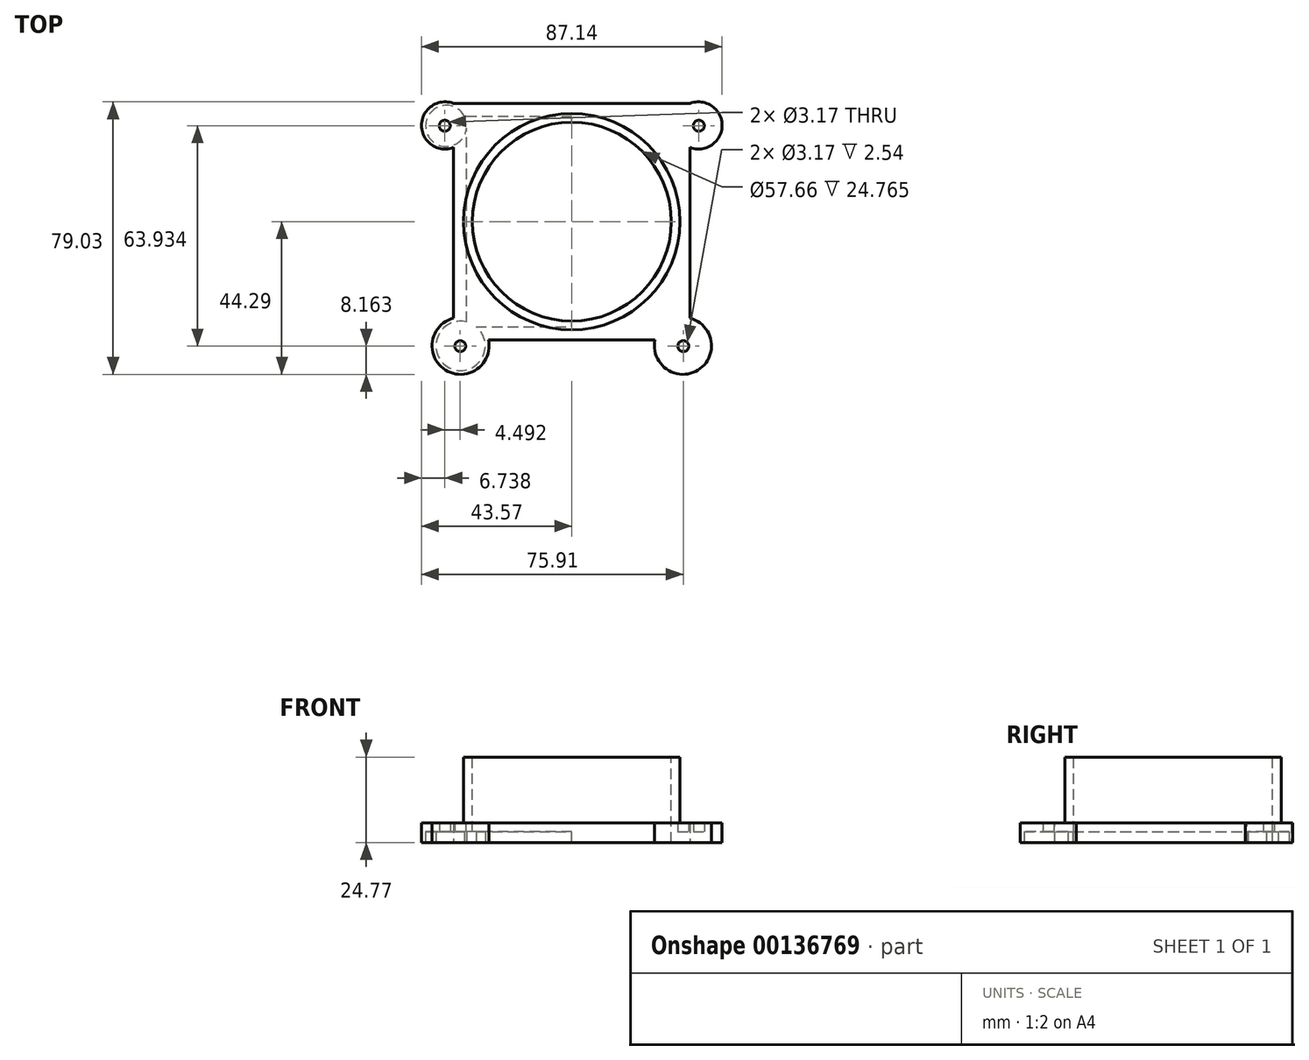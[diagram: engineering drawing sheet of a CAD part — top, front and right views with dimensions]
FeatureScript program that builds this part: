
annotation { "Feature Type Name" : "Feature", "Feature Type Description" : "" }
export const myFeature = defineFeature(function(context is Context, id is Id, definition is map)
    precondition{}
    {
        {
            var Q0;
            Q0=qCreatedBy(makeId("Top.planeOp"),FACE);
            var sketch = newSketch(context, id + "F0", { "sketchPlane" : qUnion([Q0])});
            skLineSegment(sketch, "E0", {"start": v(0, 0) * mm, "end": v(0, 31.75) * mm});
            skLineSegment(sketch, "E1", {"start": v(0, 0) * mm, "end": v(0, -31.75) * mm});
            skLineSegment(sketch, "E2", {"start": v(0, 0) * mm, "end": v(31.75, 0) * mm});
            skLineSegment(sketch, "E3", {"start": v(0, 0) * mm, "end": v(-31.75, 0) * mm});
            skLineSegment(sketch, "E4", {"start": v(0, 31.75) * mm, "end": v(-31.75, 31.75) * mm});
            skLineSegment(sketch, "E5", {"start": v(-31.75, 31.75) * mm, "end": v(-31.75, -31.75) * mm});
            skLineSegment(sketch, "E6", {"start": v(-31.75, -31.75) * mm, "end": v(31.75, -31.75) * mm});
            skLineSegment(sketch, "E7", {"start": v(31.75, -31.75) * mm, "end": v(31.75, 31.75) * mm});
            skLineSegment(sketch, "E8", {"start": v(0, 31.75) * mm, "end": v(31.75, 31.75) * mm});
            skSolve(sketch);
        }
        {
            var Q0;
            Q0 = qSketchRegion(id + "F0", true);
            extrude(context, id + "F1", {"entities" : qUnion([Q0]), "depth" : 2.54 * mm});
        }
        {
            var Q0;
            Q0=makeQuery(id+"F1.opExtrude","CAP_FACE",FACE,{"disambiguationData":[OSD([sQuery(id+"F0.wireOp",EDGE,"E4"),sQuery(id+"F0.wireOp",EDGE,"E5"),sQuery(id+"F0.wireOp",EDGE,"E6"),sQuery(id+"F0.wireOp",EDGE,"E7"),sQuery(id+"F0.wireOp",EDGE,"E8")])],"isStart":false});
            var sketch = newSketch(context, id + "F2", { "sketchPlane" : qUnion([Q0])});
            skCircle(sketch, "E9", {"center": v(0, 0) * mm, "radius": 28.83 * mm});
            skSolve(sketch);
        }
        {
            var Q0;
            Q0 = qSketchRegion(id + "F2", true);
            extrude(context, id + "F3", {"entities" : qUnion([Q0]), "operationType" : NewBodyOperationType.REMOVE, "oppositeDirection" : true, "depth" : 25.4 * mm});
        }
        {
            var Q0;
            Q0=makeQuery(id+"F1.opExtrude","SWEPT_FACE",FACE,{"disambiguationData":[OSD([sQuery(id+"F0.wireOp",EDGE,"E6")])]});
            extrude(context, id + "F4", {"entities" : qUnion([Q0]), "operationType" : NewBodyOperationType.ADD, "depth" : 2.54 * mm});
        }
        {
            var Q0;
            Q0=makeQuery(id+"F1.opExtrude","SWEPT_FACE",FACE,{"disambiguationData":[OSD([sQuery(id+"F0.wireOp",EDGE,"E4"),sQuery(id+"F0.wireOp",EDGE,"E8")])]});
            extrude(context, id + "F5", {"entities" : qUnion([Q0]), "operationType" : NewBodyOperationType.ADD, "depth" : 2.54 * mm});
        }
        {
            var Q0;
            {var subQ0=sQuery(id+"F0.wireOp",EDGE,"E7");Q0=makeQuery(id+"F5.boolean.opBoolean","MERGE",FACE,{"derivedFrom":[makeQuery(id+"F4.boolean.opBoolean","MERGE",FACE,{"derivedFrom":[makeQuery(id+"F1.opExtrude","SWEPT_FACE",FACE,{"disambiguationData":[OSD([subQ0])]}),makeQuery(id+"F4.opExtrude","SWEPT_FACE",FACE,{"disambiguationData":[OSD([sQuery(id+"F0.wireOp",EDGE,"E6"),subQ0])]})]}),makeQuery(id+"F5.opExtrude","SWEPT_FACE",FACE,{"disambiguationData":[OSD([subQ0,sQuery(id+"F0.wireOp",EDGE,"E8")])]})]});}
            extrude(context, id + "F6", {"entities" : qUnion([Q0]), "operationType" : NewBodyOperationType.ADD, "depth" : 2.54 * mm});
        }
        {
            var Q0;
            {var subQ0=sQuery(id+"F0.wireOp",EDGE,"E5");Q0=makeQuery(id+"F5.boolean.opBoolean","MERGE",FACE,{"derivedFrom":[makeQuery(id+"F4.boolean.opBoolean","MERGE",FACE,{"derivedFrom":[makeQuery(id+"F1.opExtrude","SWEPT_FACE",FACE,{"disambiguationData":[OSD([subQ0])]}),makeQuery(id+"F4.opExtrude","SWEPT_FACE",FACE,{"disambiguationData":[OSD([subQ0,sQuery(id+"F0.wireOp",EDGE,"E6")])]})]}),makeQuery(id+"F5.opExtrude","SWEPT_FACE",FACE,{"disambiguationData":[OSD([sQuery(id+"F0.wireOp",EDGE,"E4"),subQ0])]})]});}
            extrude(context, id + "F7", {"entities" : qUnion([Q0]), "operationType" : NewBodyOperationType.ADD, "depth" : 2.54 * mm});
        }
        {
            var Q0;
            {var subQ0=sQuery(id+"F0.wireOp",EDGE,"E5");var subQ1=sQuery(id+"F0.wireOp",EDGE,"E4");var subQ2=sQuery(id+"F0.wireOp",EDGE,"E6");var subQ3=sQuery(id+"F0.wireOp",EDGE,"E8");var subQ4=sQuery(id+"F0.wireOp",EDGE,"E7");Q0=makeQuery(id+"F7.boolean.opBoolean","MERGE",FACE,{"derivedFrom":[makeQuery(id+"F6.boolean.opBoolean","MERGE",FACE,{"derivedFrom":[makeQuery(id+"F5.boolean.opBoolean","MERGE",FACE,{"derivedFrom":[makeQuery(id+"F4.boolean.opBoolean","MERGE",FACE,{"derivedFrom":[makeQuery(id+"F1.opExtrude","CAP_FACE",FACE,{"disambiguationData":[OSD([subQ1,subQ0,subQ2,subQ4,subQ3])],"isStart":false}),makeQuery(id+"F4.opExtrude","SWEPT_FACE",FACE,{"disambiguationData":[OSD([subQ2]),TDD([makeQuery(id+"F1.opExtrude","CAP_EDGE",EDGE,{"disambiguationData":[OSD([subQ2])],"isStart":false})])]})]}),makeQuery(id+"F5.opExtrude","SWEPT_FACE",FACE,{"disambiguationData":[OSD([subQ1,subQ3]),TDD([makeQuery(id+"F1.opExtrude","CAP_EDGE",EDGE,{"disambiguationData":[OSD([subQ1,subQ3])],"isStart":false})])]})]}),makeQuery(id+"F6.opExtrude","SWEPT_FACE",FACE,{"disambiguationData":[OSD([subQ2,subQ4,subQ3]),TDD([makeQuery(id+"F5.boolean.opBoolean","MERGE",EDGE,{"derivedFrom":[makeQuery(id+"F4.boolean.opBoolean","MERGE",EDGE,{"derivedFrom":[makeQuery(id+"F1.opExtrude","CAP_EDGE",EDGE,{"disambiguationData":[OSD([subQ4])],"isStart":false}),makeQuery(id+"F4.opExtrude","SWEPT_EDGE",EDGE,{"disambiguationData":[OSD([subQ2,subQ4]),TDD([makeQuery(id+"F1.opExtrude","CAP_VERTEX",VERTEX,{"disambiguationData":[OSD([subQ2,subQ4])],"isStart":false})])]})]}),makeQuery(id+"F5.opExtrude","SWEPT_EDGE",EDGE,{"disambiguationData":[OSD([subQ4,subQ3]),TDD([makeQuery(id+"F1.opExtrude","CAP_VERTEX",VERTEX,{"disambiguationData":[OSD([subQ4,subQ3])],"isStart":false})])]})]})])]})]}),makeQuery(id+"F7.opExtrude","SWEPT_FACE",FACE,{"disambiguationData":[OSD([subQ1,subQ0,subQ2]),TDD([makeQuery(id+"F5.boolean.opBoolean","MERGE",EDGE,{"derivedFrom":[makeQuery(id+"F4.boolean.opBoolean","MERGE",EDGE,{"derivedFrom":[makeQuery(id+"F1.opExtrude","CAP_EDGE",EDGE,{"disambiguationData":[OSD([subQ0])],"isStart":false}),makeQuery(id+"F4.opExtrude","SWEPT_EDGE",EDGE,{"disambiguationData":[OSD([subQ0,subQ2]),TDD([makeQuery(id+"F1.opExtrude","CAP_VERTEX",VERTEX,{"disambiguationData":[OSD([subQ0,subQ2])],"isStart":false})])]})]}),makeQuery(id+"F5.opExtrude","SWEPT_EDGE",EDGE,{"disambiguationData":[OSD([subQ1,subQ0]),TDD([makeQuery(id+"F1.opExtrude","CAP_VERTEX",VERTEX,{"disambiguationData":[OSD([subQ1,subQ0])],"isStart":false})])]})]})])]})]});}
            var sketch = newSketch(context, id + "F8", { "sketchPlane" : qUnion([Q0])});
            skCircle(sketch, "E10", {"center": v(0, 0) * mm, "radius": 28.83 * mm});
            skCircle(sketch, "E11", {"center": v(0, 0) * mm, "radius": 31.37 * mm});
            skSolve(sketch);
        }
        {
            var Q0;
            Q0 = qSketchRegion(id + "F8", true);
            extrude(context, id + "F9", {"entities" : qUnion([Q0]), "operationType" : NewBodyOperationType.ADD, "depth" : 19.05 * mm});
        }
        {
            var Q0;
            Q0=makeQuery(id+"F7.opExtrude","CAP_FACE",FACE,{"disambiguationData":[OSD([sQuery(id+"F0.wireOp",EDGE,"E4"),sQuery(id+"F0.wireOp",EDGE,"E5"),sQuery(id+"F0.wireOp",EDGE,"E6")])],"isStart":false});
            cPlane(context, id + "F10", {"entities" : qUnion([Q0]), "cplaneType" : CPlaneType.OFFSET, "offset" : 34.3 * mm, "oppositeDirection" : true, "width" : 152.4 * mm, "height" : 152.4 * mm});
        }
        {
            var Q0;
            {var subQ0=sQuery(id+"F0.wireOp",EDGE,"E5");var subQ1=sQuery(id+"F0.wireOp",EDGE,"E4");var subQ2=sQuery(id+"F0.wireOp",EDGE,"E6");var subQ3=sQuery(id+"F0.wireOp",EDGE,"E8");var subQ4=sQuery(id+"F0.wireOp",EDGE,"E7");Q0=makeQuery(id+"F7.boolean.opBoolean","MERGE",FACE,{"derivedFrom":[makeQuery(id+"F6.boolean.opBoolean","MERGE",FACE,{"derivedFrom":[makeQuery(id+"F5.boolean.opBoolean","MERGE",FACE,{"derivedFrom":[makeQuery(id+"F4.boolean.opBoolean","MERGE",FACE,{"derivedFrom":[makeQuery(id+"F1.opExtrude","CAP_FACE",FACE,{"disambiguationData":[OSD([subQ1,subQ0,subQ2,subQ4,subQ3])],"isStart":false}),makeQuery(id+"F4.opExtrude","SWEPT_FACE",FACE,{"disambiguationData":[OSD([subQ2]),TDD([makeQuery(id+"F1.opExtrude","CAP_EDGE",EDGE,{"disambiguationData":[OSD([subQ2])],"isStart":false})])]})]}),makeQuery(id+"F5.opExtrude","SWEPT_FACE",FACE,{"disambiguationData":[OSD([subQ1,subQ3]),TDD([makeQuery(id+"F1.opExtrude","CAP_EDGE",EDGE,{"disambiguationData":[OSD([subQ1,subQ3])],"isStart":false})])]})]}),makeQuery(id+"F6.opExtrude","SWEPT_FACE",FACE,{"disambiguationData":[OSD([subQ2,subQ4,subQ3]),TDD([makeQuery(id+"F5.boolean.opBoolean","MERGE",EDGE,{"derivedFrom":[makeQuery(id+"F4.boolean.opBoolean","MERGE",EDGE,{"derivedFrom":[makeQuery(id+"F1.opExtrude","CAP_EDGE",EDGE,{"disambiguationData":[OSD([subQ4])],"isStart":false}),makeQuery(id+"F4.opExtrude","SWEPT_EDGE",EDGE,{"disambiguationData":[OSD([subQ2,subQ4]),TDD([makeQuery(id+"F1.opExtrude","CAP_VERTEX",VERTEX,{"disambiguationData":[OSD([subQ2,subQ4])],"isStart":false})])]})]}),makeQuery(id+"F5.opExtrude","SWEPT_EDGE",EDGE,{"disambiguationData":[OSD([subQ4,subQ3]),TDD([makeQuery(id+"F1.opExtrude","CAP_VERTEX",VERTEX,{"disambiguationData":[OSD([subQ4,subQ3])],"isStart":false})])]})]})])]})]}),makeQuery(id+"F7.opExtrude","SWEPT_FACE",FACE,{"disambiguationData":[OSD([subQ1,subQ0,subQ2]),TDD([makeQuery(id+"F5.boolean.opBoolean","MERGE",EDGE,{"derivedFrom":[makeQuery(id+"F4.boolean.opBoolean","MERGE",EDGE,{"derivedFrom":[makeQuery(id+"F1.opExtrude","CAP_EDGE",EDGE,{"disambiguationData":[OSD([subQ0])],"isStart":false}),makeQuery(id+"F4.opExtrude","SWEPT_EDGE",EDGE,{"disambiguationData":[OSD([subQ0,subQ2]),TDD([makeQuery(id+"F1.opExtrude","CAP_VERTEX",VERTEX,{"disambiguationData":[OSD([subQ0,subQ2])],"isStart":false})])]})]}),makeQuery(id+"F5.opExtrude","SWEPT_EDGE",EDGE,{"disambiguationData":[OSD([subQ1,subQ0]),TDD([makeQuery(id+"F1.opExtrude","CAP_VERTEX",VERTEX,{"disambiguationData":[OSD([subQ1,subQ0])],"isStart":false})])]})]})])]})]});}
            var sketch = newSketch(context, id + "F11", { "sketchPlane" : qUnion([Q0])});
            skArc(sketch, "E12", {"start": v(24.16, -34.3) * mm, "mid": v(36.6, -43.05) * mm, "end": v(34.3, -28.01) * mm});
            skSolve(sketch);
        }
        {
            var Q0;
            Q0 = qSketchRegion(id + "F11", true);
            var Q1;
            {var subQ0=sQuery(id+"F11.wireOp",EDGE,"E12");Q1=makeQuery(id+"F11.imprint","IMPRINT",FACE,{"disambiguationData":[TD([[makeQuery(id+"F11.imprint","IMPRINT",EDGE,{"derivedFrom":subQ0}),1.0]])]});}
            extrude(context, id + "F12", {"entities" : qUnion([Q0, Q1]), "oppositeDirection" : true, "depth" : 2.54 * mm});
        }
        {
            var Q0;
            Q0=makeQuery(id+"F12.opExtrude","SWEPT_BODY",BODY,{"disambiguationData":[OSD([sQuery(id+"F0.wireOp",EDGE,"E5"),sQuery(id+"F0.wireOp",EDGE,"E6"),sQuery(id+"F0.wireOp",EDGE,"E7"),sQuery(id+"F0.wireOp",EDGE,"E8"),sQuery(id+"F11.wireOp",EDGE,"E12")])]});
            var Q1;
            Q1=qCreatedBy(id+"F10.planeOp",FACE);
            mirror(context, id + "F13", {"operationType" : NewBodyOperationType.ADD, "entities" : qUnion([Q0]), "mirrorPlane" : qUnion([Q1])});
        }
        {
            var Q0;
            {var subQ0=sQuery(id+"F0.wireOp",EDGE,"E8");var subQ1=sQuery(id+"F0.wireOp",EDGE,"E7");var subQ2=sQuery(id+"F0.wireOp",EDGE,"E6");var subQ3=sQuery(id+"F0.wireOp",EDGE,"E5");var subQ4=makeQuery(id+"F12.opExtrude","CAP_FACE",FACE,{"disambiguationData":[OSD([subQ3,subQ2,subQ1,subQ0,sQuery(id+"F11.wireOp",EDGE,"E12")])],"isStart":true});var subQ5=sQuery(id+"F0.wireOp",EDGE,"E4");Q0=makeQuery(id+"F13.boolean.opBoolean","MERGE",FACE,{"derivedFrom":[makeQuery(id+"F7.boolean.opBoolean","MERGE",FACE,{"derivedFrom":[makeQuery(id+"F6.boolean.opBoolean","MERGE",FACE,{"derivedFrom":[makeQuery(id+"F5.boolean.opBoolean","MERGE",FACE,{"derivedFrom":[makeQuery(id+"F4.boolean.opBoolean","MERGE",FACE,{"derivedFrom":[makeQuery(id+"F1.opExtrude","CAP_FACE",FACE,{"disambiguationData":[OSD([subQ5,subQ3,subQ2,subQ1,subQ0])],"isStart":false}),makeQuery(id+"F4.opExtrude","SWEPT_FACE",FACE,{"disambiguationData":[OSD([subQ2]),TDD([makeQuery(id+"F1.opExtrude","CAP_EDGE",EDGE,{"disambiguationData":[OSD([subQ2])],"isStart":false})])]})]}),makeQuery(id+"F5.opExtrude","SWEPT_FACE",FACE,{"disambiguationData":[OSD([subQ5,subQ0]),TDD([makeQuery(id+"F1.opExtrude","CAP_EDGE",EDGE,{"disambiguationData":[OSD([subQ5,subQ0])],"isStart":false})])]})]}),makeQuery(id+"F6.opExtrude","SWEPT_FACE",FACE,{"disambiguationData":[OSD([subQ2,subQ1,subQ0]),TDD([makeQuery(id+"F5.boolean.opBoolean","MERGE",EDGE,{"derivedFrom":[makeQuery(id+"F4.boolean.opBoolean","MERGE",EDGE,{"derivedFrom":[makeQuery(id+"F1.opExtrude","CAP_EDGE",EDGE,{"disambiguationData":[OSD([subQ1])],"isStart":false}),makeQuery(id+"F4.opExtrude","SWEPT_EDGE",EDGE,{"disambiguationData":[OSD([subQ2,subQ1]),TDD([makeQuery(id+"F1.opExtrude","CAP_VERTEX",VERTEX,{"disambiguationData":[OSD([subQ2,subQ1])],"isStart":false})])]})]}),makeQuery(id+"F5.opExtrude","SWEPT_EDGE",EDGE,{"disambiguationData":[OSD([subQ1,subQ0]),TDD([makeQuery(id+"F1.opExtrude","CAP_VERTEX",VERTEX,{"disambiguationData":[OSD([subQ1,subQ0])],"isStart":false})])]})]})])]})]}),makeQuery(id+"F7.opExtrude","SWEPT_FACE",FACE,{"disambiguationData":[OSD([subQ5,subQ3,subQ2]),TDD([makeQuery(id+"F5.boolean.opBoolean","MERGE",EDGE,{"derivedFrom":[makeQuery(id+"F4.boolean.opBoolean","MERGE",EDGE,{"derivedFrom":[makeQuery(id+"F1.opExtrude","CAP_EDGE",EDGE,{"disambiguationData":[OSD([subQ3])],"isStart":false}),makeQuery(id+"F4.opExtrude","SWEPT_EDGE",EDGE,{"disambiguationData":[OSD([subQ3,subQ2]),TDD([makeQuery(id+"F1.opExtrude","CAP_VERTEX",VERTEX,{"disambiguationData":[OSD([subQ3,subQ2])],"isStart":false})])]})]}),makeQuery(id+"F5.opExtrude","SWEPT_EDGE",EDGE,{"disambiguationData":[OSD([subQ5,subQ3]),TDD([makeQuery(id+"F1.opExtrude","CAP_VERTEX",VERTEX,{"disambiguationData":[OSD([subQ5,subQ3])],"isStart":false})])]})]})])]})]}),subQ4,makeQuery(id+"F13.opPattern","COPY",FACE,{"derivedFrom":subQ4,"instanceName":"1"})]});}
            var sketch = newSketch(context, id + "F14", { "sketchPlane" : qUnion([Q0])});
            skArc(sketch, "E13", {"start": v(34.3, 21.5) * mm, "mid": v(43.57, 27.9) * mm, "end": v(34.3, 34.3) * mm});
            skSolve(sketch);
        }
        {
            var Q0;
            {var subQ0=sQuery(id+"F14.wireOp",EDGE,"E13");Q0=makeQuery(id+"F14.imprint","IMPRINT",FACE,{"disambiguationData":[TD([[makeQuery(id+"F14.imprint","IMPRINT",EDGE,{"derivedFrom":subQ0}),1.0]])]});}
            extrude(context, id + "F15", {"entities" : qUnion([Q0]), "oppositeDirection" : true, "depth" : 2.54 * mm});
        }
        {
            var Q0;
            Q0=makeQuery(id+"F15.opExtrude","SWEPT_BODY",BODY,{"disambiguationData":[OSD([sQuery(id+"F0.wireOp",EDGE,"E6"),sQuery(id+"F0.wireOp",EDGE,"E7"),sQuery(id+"F0.wireOp",EDGE,"E8"),sQuery(id+"F14.wireOp",EDGE,"E13")])]});
            var Q1;
            Q1=qCreatedBy(id+"F10.planeOp",FACE);
            mirror(context, id + "F16", {"operationType" : NewBodyOperationType.ADD, "entities" : qUnion([Q0]), "mirrorPlane" : qUnion([Q1])});
        }
        {
            var Q0;
            {var subQ0=sQuery(id+"F0.wireOp",EDGE,"E8");var subQ1=sQuery(id+"F0.wireOp",EDGE,"E7");var subQ2=sQuery(id+"F0.wireOp",EDGE,"E6");var subQ3=makeQuery(id+"F15.opExtrude","CAP_FACE",FACE,{"disambiguationData":[OSD([subQ2,subQ1,subQ0,sQuery(id+"F14.wireOp",EDGE,"E13")])],"isStart":false});var subQ4=sQuery(id+"F0.wireOp",EDGE,"E5");var subQ5=makeQuery(id+"F12.opExtrude","CAP_FACE",FACE,{"disambiguationData":[OSD([subQ4,subQ2,subQ1,subQ0,sQuery(id+"F11.wireOp",EDGE,"E12")])],"isStart":false});var subQ6=sQuery(id+"F0.wireOp",EDGE,"E4");Q0=makeQuery(id+"F16.boolean.opBoolean","MERGE",FACE,{"derivedFrom":[makeQuery(id+"F13.boolean.opBoolean","MERGE",FACE,{"derivedFrom":[makeQuery(id+"F7.boolean.opBoolean","MERGE",FACE,{"derivedFrom":[makeQuery(id+"F6.boolean.opBoolean","MERGE",FACE,{"derivedFrom":[makeQuery(id+"F5.boolean.opBoolean","MERGE",FACE,{"derivedFrom":[makeQuery(id+"F4.boolean.opBoolean","MERGE",FACE,{"derivedFrom":[makeQuery(id+"F1.opExtrude","CAP_FACE",FACE,{"disambiguationData":[OSD([subQ6,subQ4,subQ2,subQ1,subQ0])],"isStart":true}),makeQuery(id+"F4.opExtrude","SWEPT_FACE",FACE,{"disambiguationData":[OSD([subQ2]),TDD([makeQuery(id+"F1.opExtrude","CAP_EDGE",EDGE,{"disambiguationData":[OSD([subQ2])],"isStart":true})])]})]}),makeQuery(id+"F5.opExtrude","SWEPT_FACE",FACE,{"disambiguationData":[OSD([subQ6,subQ0]),TDD([makeQuery(id+"F1.opExtrude","CAP_EDGE",EDGE,{"disambiguationData":[OSD([subQ6,subQ0])],"isStart":true})])]})]}),makeQuery(id+"F6.opExtrude","SWEPT_FACE",FACE,{"disambiguationData":[OSD([subQ2,subQ1,subQ0]),TDD([makeQuery(id+"F5.boolean.opBoolean","MERGE",EDGE,{"derivedFrom":[makeQuery(id+"F4.boolean.opBoolean","MERGE",EDGE,{"derivedFrom":[makeQuery(id+"F1.opExtrude","CAP_EDGE",EDGE,{"disambiguationData":[OSD([subQ1])],"isStart":true}),makeQuery(id+"F4.opExtrude","SWEPT_EDGE",EDGE,{"disambiguationData":[OSD([subQ2,subQ1]),TDD([makeQuery(id+"F1.opExtrude","CAP_VERTEX",VERTEX,{"disambiguationData":[OSD([subQ2,subQ1])],"isStart":true})])]})]}),makeQuery(id+"F5.opExtrude","SWEPT_EDGE",EDGE,{"disambiguationData":[OSD([subQ1,subQ0]),TDD([makeQuery(id+"F1.opExtrude","CAP_VERTEX",VERTEX,{"disambiguationData":[OSD([subQ1,subQ0])],"isStart":true})])]})]})])]})]}),makeQuery(id+"F7.opExtrude","SWEPT_FACE",FACE,{"disambiguationData":[OSD([subQ6,subQ4,subQ2]),TDD([makeQuery(id+"F5.boolean.opBoolean","MERGE",EDGE,{"derivedFrom":[makeQuery(id+"F4.boolean.opBoolean","MERGE",EDGE,{"derivedFrom":[makeQuery(id+"F1.opExtrude","CAP_EDGE",EDGE,{"disambiguationData":[OSD([subQ4])],"isStart":true}),makeQuery(id+"F4.opExtrude","SWEPT_EDGE",EDGE,{"disambiguationData":[OSD([subQ4,subQ2]),TDD([makeQuery(id+"F1.opExtrude","CAP_VERTEX",VERTEX,{"disambiguationData":[OSD([subQ4,subQ2])],"isStart":true})])]})]}),makeQuery(id+"F5.opExtrude","SWEPT_EDGE",EDGE,{"disambiguationData":[OSD([subQ6,subQ4]),TDD([makeQuery(id+"F1.opExtrude","CAP_VERTEX",VERTEX,{"disambiguationData":[OSD([subQ6,subQ4])],"isStart":true})])]})]})])]})]}),subQ5,makeQuery(id+"F13.opPattern","COPY",FACE,{"derivedFrom":subQ5,"instanceName":"1"})]}),subQ3,makeQuery(id+"F16.opPattern","COPY",FACE,{"derivedFrom":subQ3,"instanceName":"1"})]});}
            extrude(context, id + "F17", {"entities" : qUnion([Q0]), "operationType" : NewBodyOperationType.ADD, "depth" : 3.17 * mm});
        }
        {
            var Q0;
            Q0=makeQuery(id+"F17.opExtrude","CAP_FACE",FACE,{"disambiguationData":[OSD([sQuery(id+"F0.wireOp",EDGE,"E4"),sQuery(id+"F0.wireOp",EDGE,"E5"),sQuery(id+"F0.wireOp",EDGE,"E6"),sQuery(id+"F0.wireOp",EDGE,"E7"),sQuery(id+"F0.wireOp",EDGE,"E8"),sQuery(id+"F11.wireOp",EDGE,"E12"),sQuery(id+"F14.wireOp",EDGE,"E13")])],"isStart":false});
            var sketch = newSketch(context, id + "F18", { "sketchPlane" : qUnion([Q0])});
            skLineSegment(sketch, "E14", {"start": v(0, 34.3) * mm, "end": v(0, 30.48) * mm});
            skLineSegment(sketch, "E15", {"start": v(-27.73, 30.48) * mm, "end": v(0, 30.48) * mm});
            skLineSegment(sketch, "E16", {"start": v(-30.48, 29.1) * mm, "end": v(-30.48, -27.12) * mm});
            skLineSegment(sketch, "E17", {"start": v(-34.3, 3.25) * mm, "end": v(-30.48, 3.25) * mm});
            skLineSegment(sketch, "E18", {"start": v(0, 30.48) * mm, "end": v(0, -30.48) * mm});
            skPoint(sketch, "E18.endSnap0", {"position": v(0, -34.29) * mm});
            skLineSegment(sketch, "E19", {"start": v(0, -30.48) * mm, "end": v(0, -34.29) * mm});
            skLineSegment(sketch, "E20", {"start": v(0, -30.48) * mm, "end": v(-31.1, -30.48) * mm});
            skArc(sketch, "E21", {"start": v(-27.73, 30.48) * mm, "mid": v(-35.45, 42.42) * mm, "end": v(-30.48, 29.1) * mm});
            skArc(sketch, "E22", {"start": v(-30.48, -27.12) * mm, "mid": v(-42.28, -26.7) * mm, "end": v(-31.1, -30.48) * mm});
            skSolve(sketch);
        }
        {
            var Q0;
            Q0 = qSketchRegion(id + "F18", true);
            extrude(context, id + "F19", {"entities" : qUnion([Q0]), "operationType" : NewBodyOperationType.REMOVE, "oppositeDirection" : true, "depth" : 3.17 * mm});
        }
        {
            var Q0;
            {var subQ0=sQuery(id+"F18.wireOp",EDGE,"mxPTQLXm-6kJp-nk1f-0FaH-oOzNXkjwgTY7");var subQ1=sQuery(id+"F18.wireOp",EDGE,"E20");var subQ2=sQuery(id+"F18.wireOp",EDGE,"E18");var subQ3=sQuery(id+"F18.wireOp",EDGE,"6GyYETIu-Keux-k6vV-MwpU-kTG4aGo0dqZO");var subQ4=sQuery(id+"F18.wireOp",EDGE,"E16");var subQ5=sQuery(id+"F18.wireOp",EDGE,"E15");Q0=makeQuery(id+"Ft3Sa1DPg6oScsn_2.1.F19.boolean.opBoolean","MERGE",FACE,{"derivedFrom":[makeQuery(id+"F19.boolean.opBoolean","COPY",FACE,{"derivedFrom":makeQuery(id+"F19.opExtrude","CAP_FACE",FACE,{"disambiguationData":[OSD([subQ5,subQ4,subQ3,subQ2,subQ1,subQ0])],"isStart":false})}),makeQuery(id+"Ft3Sa1DPg6oScsn_2.1.F19.opExtrude","CAP_FACE",FACE,{"disambiguationData":[OSD([subQ5,subQ4,subQ3,subQ2,subQ1,subQ0])],"isStart":false})]});}
            var sketch = newSketch(context, id + "F20", { "sketchPlane" : qUnion([Q0])});
            skCircle(sketch, "E23", {"center": v(-32.34, 36.13) * mm, "radius": 1.59 * mm});
            skCircle(sketch, "E24", {"center": v(32.34, 36.13) * mm, "radius": 1.59 * mm});
            skCircle(sketch, "E25", {"center": v(36.83, -27.8) * mm, "radius": 1.59 * mm});
            skCircle(sketch, "E26", {"center": v(-36.83, -27.8) * mm, "radius": 1.59 * mm});
            skSolve(sketch);
        }
        {
            var Q0;
            Q0 = qSketchRegion(id + "F20", true);
            extrude(context, id + "F21", {"entities" : qUnion([Q0]), "operationType" : NewBodyOperationType.REMOVE, "oppositeDirection" : true, "depth" : 25.4 * mm});
        }
    });
